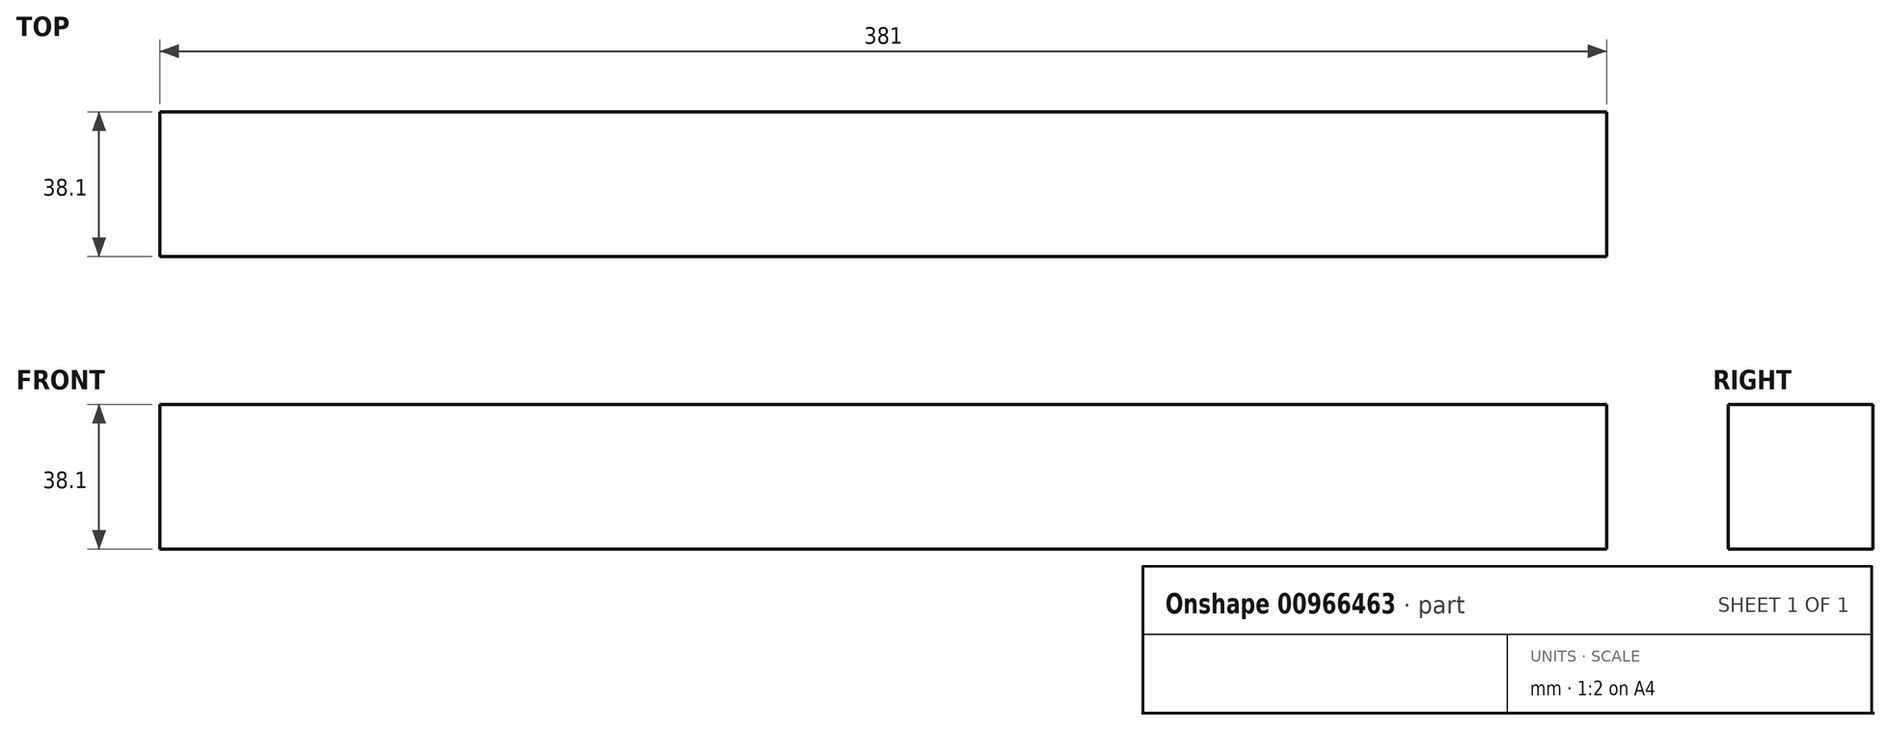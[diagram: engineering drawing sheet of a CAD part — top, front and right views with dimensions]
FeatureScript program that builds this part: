
annotation { "Feature Type Name" : "Feature", "Feature Type Description" : "" }
export const myFeature = defineFeature(function(context is Context, id is Id, definition is map)
    precondition{}
    {
        {
            var Q0;
            Q0=qCreatedBy(makeId("Front.planeOp"),FACE);
            var sketch = newSketch(context, id + "F0", { "sketchPlane" : qUnion([Q0])});
            skLineSegment(sketch, "E0.bottom", {"start": v(190.5, -19.05) * mm, "end": v(-190.5, -19.05) * mm});
            skLineSegment(sketch, "E0.top", {"start": v(190.5, 19.05) * mm, "end": v(-190.5, 19.05) * mm});
            skLineSegment(sketch, "E0.left", {"start": v(190.5, -19.05) * mm, "end": v(190.5, 19.05) * mm});
            skLineSegment(sketch, "E0.right", {"start": v(-190.5, -19.05) * mm, "end": v(-190.5, 19.05) * mm});
            skPoint(sketch, "E0.middle", {"position": v(0, 0) * mm});
            skSolve(sketch);
        }
        {
            var Q0;
            Q0 = qSketchRegion(id + "F0", true);
            extrude(context, id + "F1", {"entities" : qUnion([Q0]), "depth" : 38.1 * mm, "offsetDistance" : 25.4 * mm});
        }
    });
